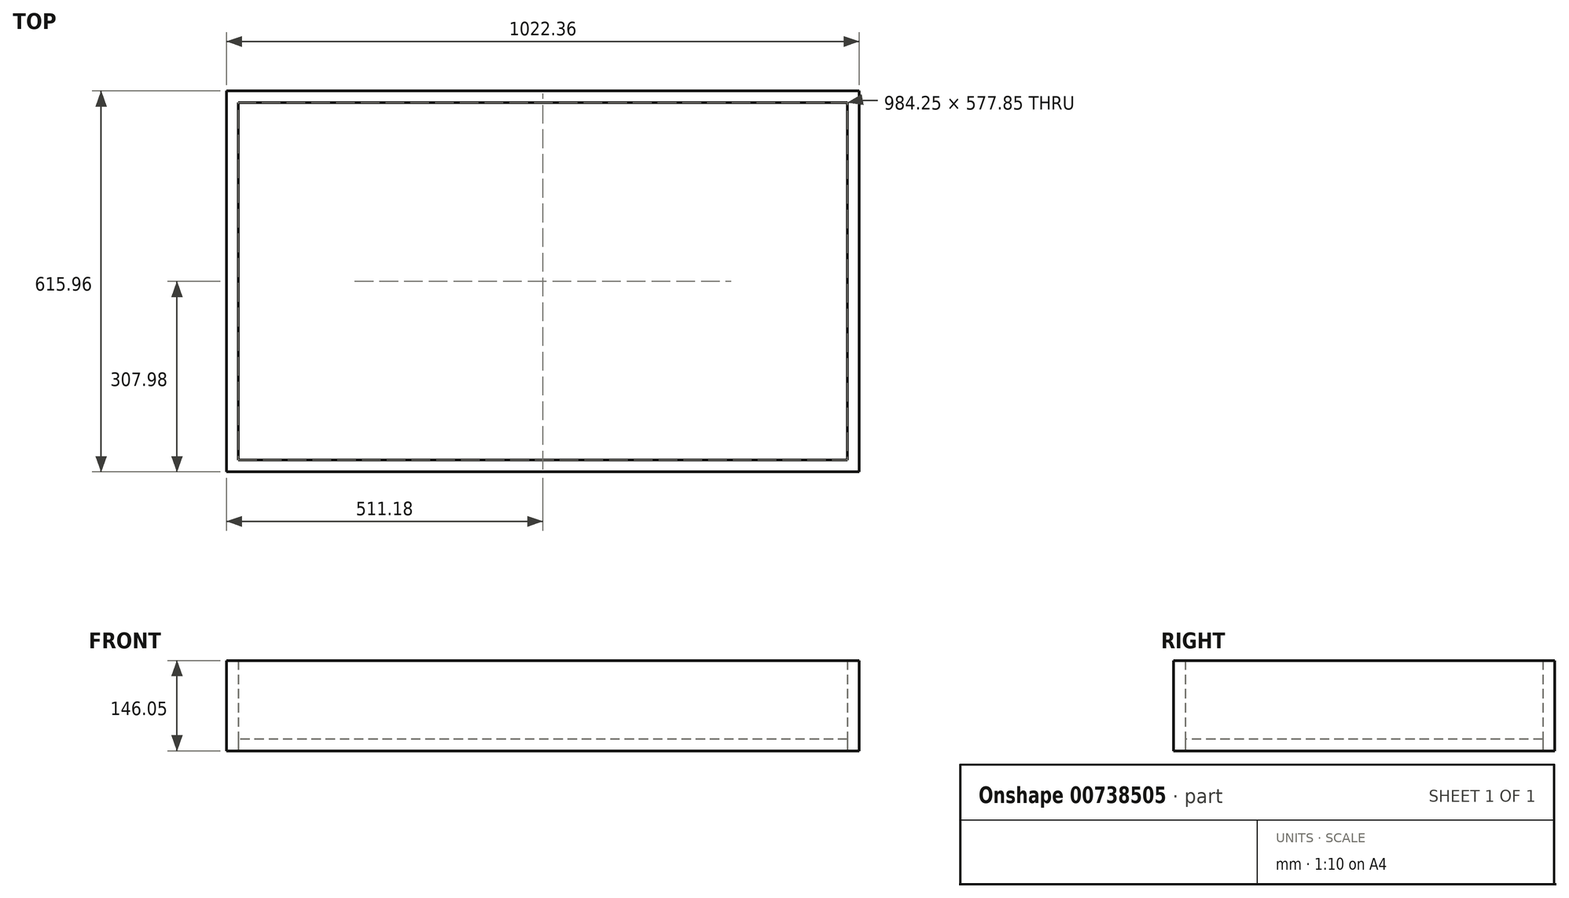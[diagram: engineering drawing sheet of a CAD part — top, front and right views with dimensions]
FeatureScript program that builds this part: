
annotation { "Feature Type Name" : "Feature", "Feature Type Description" : "" }
export const myFeature = defineFeature(function(context is Context, id is Id, definition is map)
    precondition{}
    {
        {
            var Q0;
            Q0=qCreatedBy(makeId("Top.planeOp"),FACE);
            var sketch = newSketch(context, id + "F0", { "sketchPlane" : qUnion([Q0])});
            skLineSegment(sketch, "E0.bottom", {"start": v(492.13, 288.93) * mm, "end": v(-492.12, 288.93) * mm});
            skLineSegment(sketch, "E0.top", {"start": v(492.13, -288.93) * mm, "end": v(-492.13, -288.93) * mm});
            skLineSegment(sketch, "E0.left", {"start": v(492.13, 288.93) * mm, "end": v(492.13, -288.93) * mm});
            skLineSegment(sketch, "E0.right", {"start": v(-492.13, 288.93) * mm, "end": v(-492.13, -288.93) * mm});
            skPoint(sketch, "E0.middle", {"position": v(0, 0) * mm});
            skSolve(sketch);
        }
        {
            var Q0;
            Q0 = qSketchRegion(id + "F0", true);
            extrude(context, id + "F1", {"entities" : qUnion([Q0]), "depth" : 19.05 * mm, "offsetDistance" : 25.4 * mm});
        }
        {
            var Q0;
            Q0=makeQuery(id+"F1.opExtrude","CAP_FACE",FACE,{"disambiguationData":[OSD([sQuery(id+"F0.wireOp",EDGE,"E0.bottom"),sQuery(id+"F0.wireOp",EDGE,"E0.top"),sQuery(id+"F0.wireOp",EDGE,"E0.left"),sQuery(id+"F0.wireOp",EDGE,"E0.right")])],"isStart":true});
            var sketch = newSketch(context, id + "F2", { "sketchPlane" : qUnion([Q0])});
            skLineSegment(sketch, "E1.bottom", {"start": v(-492.13, 288.93) * mm, "end": v(492.13, 288.93) * mm});
            skLineSegment(sketch, "E1.top", {"start": v(-492.13, -288.93) * mm, "end": v(492.13, -288.93) * mm});
            skLineSegment(sketch, "E1.left", {"start": v(-492.13, 288.93) * mm, "end": v(-492.13, -288.93) * mm});
            skLineSegment(sketch, "E1.right", {"start": v(492.13, 288.93) * mm, "end": v(492.13, -288.93) * mm});
            skLineSegment(sketch, "E2.0", {"start": v(-511.18, -307.98) * mm, "end": v(511.18, -307.98) * mm});
            skLineSegment(sketch, "E2.1", {"start": v(-511.18, 307.98) * mm, "end": v(-511.18, -307.98) * mm});
            skLineSegment(sketch, "E2.2", {"start": v(-511.18, 307.98) * mm, "end": v(511.18, 307.98) * mm});
            skLineSegment(sketch, "E2.3", {"start": v(511.18, 307.98) * mm, "end": v(511.18, -307.98) * mm});
            skSolve(sketch);
        }
        {
            var Q0;
            Q0 = qSketchRegion(id + "F2", true);
            extrude(context, id + "F3", {"entities" : qUnion([Q0]), "oppositeDirection" : true, "depth" : 146.05 * mm, "offsetDistance" : 25.4 * mm});
        }
    });
